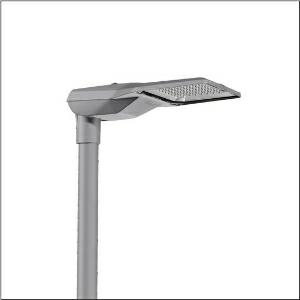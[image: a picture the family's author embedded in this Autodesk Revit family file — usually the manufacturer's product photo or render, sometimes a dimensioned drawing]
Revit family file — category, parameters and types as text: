
# Revit family: streetlight_sl_21_midi___pl52_5xe3h33s08lb_2890
name_source: partatom
category: Lighting Fixtures
units: mm (PartAtom-declared; Revit-internal decimal feet)

## family parameters
Cut with Voids When Loaded = No
Host = Face
Light Source = No
Part Type = Normal
Room Calculation Point = No
Round Connector Dimension = Use Diameter
Shared = No

## types (1)
- --- (1 x LED, 14100 lm, 99.6 W, 3000K)
    Apparent Load = 100 VA
    CIE Flux Codes = 27 59 98 100 100
    Color Rendering = 70
    Color Temperature = 3000K
    Default Elevation = 1800 mm
    Description = Streetlight SL 21 midi, mast luminaire, primary light control with lens, of PMMA, primary optical cover: cover, of toughened safety glass, transparent, light distribution: PL52, light emission: direct distribution, primary light characteristic: asymmetric, installation type: side-entry, post-top, LED, High Power LED, rated luminous flux: 14.100lm, luminous efficacy: 142lm/W, light colour: 730, colour temperature: 3000K, control gear: D4i, control: overheat protection, constant luminous flux control, time-dependent luminous flux control, flexible luminous flux parameterisation, pre-setting: logarithmic dimming characteristic, mains connection: 230..240V, AC, 50/60Hz, start of lifetime: 100W, end of service life: 102W, reduction: 46W, luminaire housing, of diecast aluminium, powder-coated, SITECO metallic grey (DB 702S), corrosivity category C5 high according to DIN EN ISO 12944, please order mast flange separately, inclination adjustable: 0°, 5°, 10°, 15°, sealing non-destructively replaceable, multi-level sealing system, length: 644mm, width: 335mm, height: 110mm, mast flange for spigot size: 42mm (side-entry): 5XC10008XM4, 60/48mm (side-entry/post-top): 5XC10108XM2, 76/60mm (side-entry/post-top): 5XC10108XM1, mounting height: 4..8m, Smart Interface above, protection rating (complete): IP66, insulation class (complete): insulation class II (safety insulation), certification: CE, ENEC, ENEC+, VDE, impact resistance: IK10, permissible operating ambient temperature for outdoor applications: -40..+50°C, standard-compliant lighting for roads and squares, packaging unit: 1 piece

Light Distribution: PL52
    Height = 111 mm
    Lamp = 1 x LED
    Lamp Light Flux = 14100 lm
    Lamp Power = 99.6 W
    Lamp count = 1
    Length = 644 mm
    Luminous efficacy = 142 lm/W
    Manufacturer = Siteco
    ModVariant = No
    Model = 5XE3H33S08LB
    Number of Poles = 1
    OnlyDefault = Yes
    Power Factor = 1
    Product Name = Streetlight SL 21 midi | PL52
    Product group = mast luminaire | pylon top
    ProductGroupID = 6100
    Protection Class = Protection class II
    Protection Degree = IP 66
    RLX_Detail_Level = 1
    RLX_Emergency_Light_Flux = 0 lm
    RLX_Emergency_Type = 0
    RLX_Emergency_Type_DB = No
    RlxData = <blob elided: 36493 chars, md5=888ccdc0>
    Socket = socket
    Standby Power = 0 W
    System Light Flux = 14100 lm
    System Power = 100 W
    Type Comments = factory setting: luminous flux: 100 % | dim-lin: 254 | 1020 mA
    Type Image = l_1004302.jpg
    URL = http://relux.com
    VarID = @adj_032185
    Voltage = 0 V
    Weight = 0.00 kg
    Width = 336 mm

## geometry (parser evidence)
native form markers: Blend x4, Sweep x11
no freeform markers — native parametric forms only
